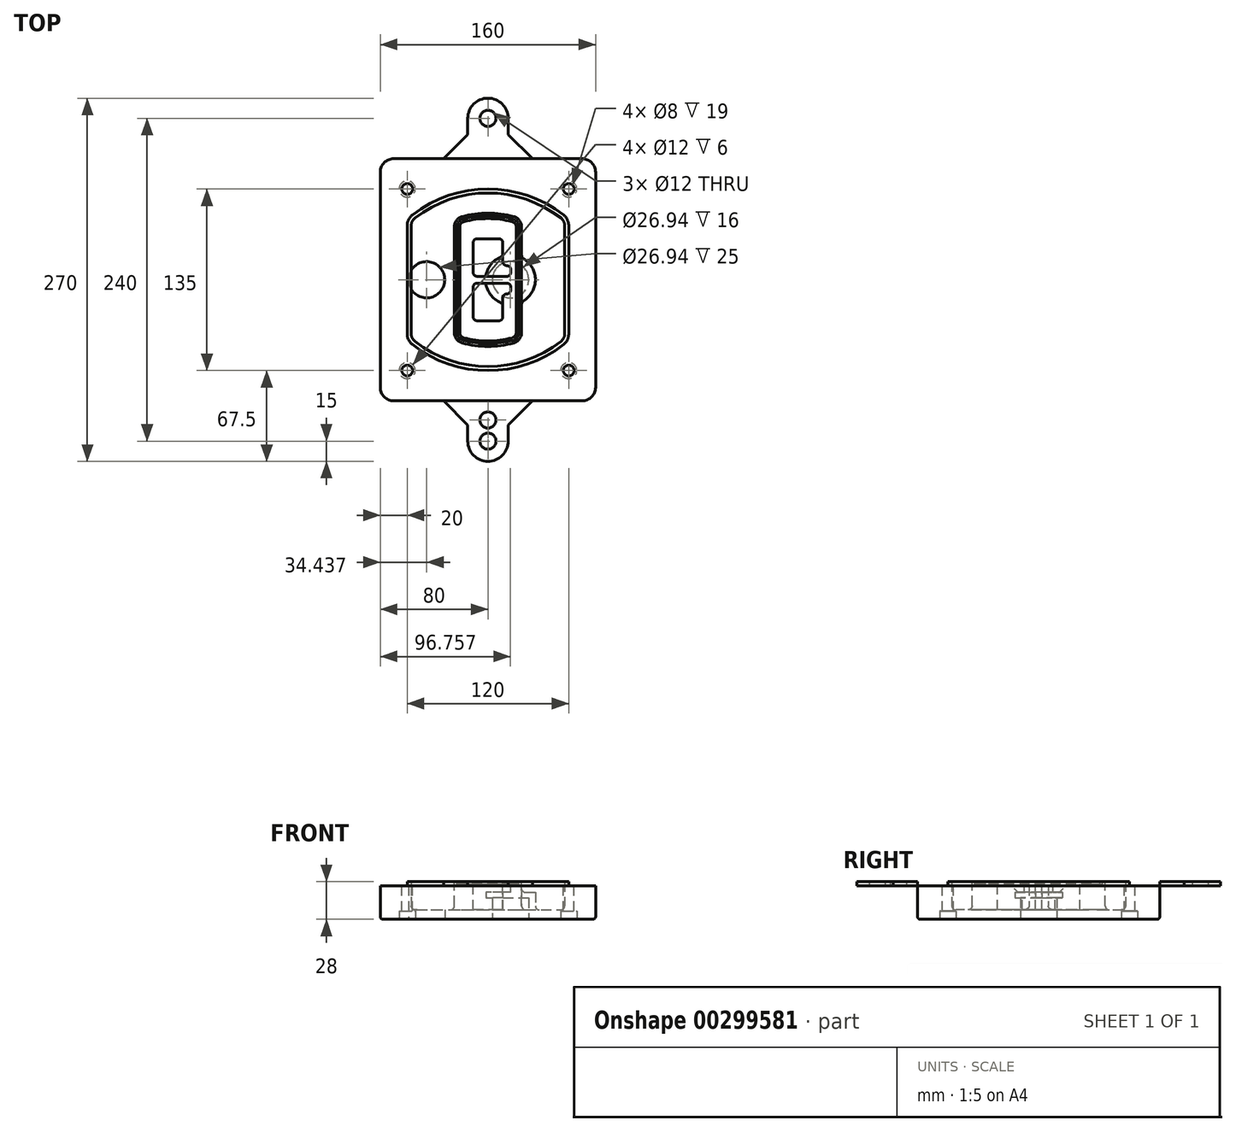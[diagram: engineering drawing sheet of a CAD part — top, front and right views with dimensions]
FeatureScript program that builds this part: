
annotation { "Feature Type Name" : "Feature", "Feature Type Description" : "" }
export const myFeature = defineFeature(function(context is Context, id is Id, definition is map)
    precondition{}
    {
        {
            var Q0;
            Q0=qCreatedBy(makeId("Top.planeOp"),FACE);
            var sketch = newSketch(context, id + "F0", { "sketchPlane" : qUnion([Q0])});
            skPoint(sketch, "E0.rect.middle", {"position": v(0, 0) * mm});
            skLineSegment(sketch, "E1.bottom", {"start": v(-70, -90) * mm, "end": v(70, -90) * mm});
            skLineSegment(sketch, "E1.top", {"start": v(-70, 90) * mm, "end": v(70, 90) * mm});
            skLineSegment(sketch, "E1.left", {"start": v(-80, -80) * mm, "end": v(-80, 80) * mm});
            skLineSegment(sketch, "E1.right", {"start": v(80, -80) * mm, "end": v(80, 80) * mm});
            skLineSegment(sketch, "E2", {"start": v(-80, 90) * mm, "end": v(80, -90) * mm, "construction": true});
            skLineSegment(sketch, "E3", {"start": v(80, 90) * mm, "end": v(-80, -90) * mm, "construction": true});
            skCircle(sketch, "E4", {"center": v(-60, 67.5) * mm, "radius": 4 * mm});
            skCircle(sketch, "E5", {"center": v(60, 67.5) * mm, "radius": 4 * mm});
            skCircle(sketch, "E6", {"center": v(60, -67.5) * mm, "radius": 4 * mm});
            skCircle(sketch, "E7", {"center": v(-60, -67.5) * mm, "radius": 4 * mm});
            skLineSegment(sketch, "E8", {"start": v(-60, 67.5) * mm, "end": v(60, 67.5) * mm, "construction": true});
            skLineSegment(sketch, "E9", {"start": v(60, 67.5) * mm, "end": v(60, -67.5) * mm, "construction": true});
            skLineSegment(sketch, "E10", {"start": v(60, -67.5) * mm, "end": v(-60, -67.5) * mm, "construction": true});
            skLineSegment(sketch, "E11", {"start": v(-60, -67.5) * mm, "end": v(-60, 67.5) * mm, "construction": true});
            skLineSegment(sketch, "E12", {"start": v(-60, 40.3) * mm, "end": v(-60, -40.3) * mm});
            skLineSegment(sketch, "E13", {"start": v(60, 40.3) * mm, "end": v(60, -40.3) * mm});
            skArc(sketch, "E14", {"start": v(56.15, 48.18) * mm, "mid": v(0, 67.5) * mm, "end": v(-56.15, 48.18) * mm});
            skArc(sketch, "E15", {"start": v(-56.15, -48.18) * mm, "mid": v(0, -67.5) * mm, "end": v(56.15, -48.18) * mm});
            skLineSegment(sketch, "E16", {"start": v(-60, 0) * mm, "end": v(60, 0) * mm, "construction": true});
            skPoint(sketch, "E17.visualSharp", {"position": v(-60, -45) * mm});
            skArc(sketch, "E17.filletArc", {"start": v(-60, -40.3) * mm, "mid": v(-58.99, -44.68) * mm, "end": v(-56.15, -48.18) * mm});
            skPoint(sketch, "E18.visualSharp", {"position": v(-60, 45) * mm});
            skArc(sketch, "E18.filletArc", {"start": v(-56.15, 48.18) * mm, "mid": v(-58.99, 44.68) * mm, "end": v(-60, 40.3) * mm});
            skPoint(sketch, "E19.visualSharp", {"position": v(60, 45) * mm});
            skArc(sketch, "E19.filletArc", {"start": v(60, 40.3) * mm, "mid": v(58.99, 44.68) * mm, "end": v(56.15, 48.18) * mm});
            skPoint(sketch, "E20.visualSharp", {"position": v(60, -45) * mm});
            skArc(sketch, "E20.filletArc", {"start": v(56.15, -48.18) * mm, "mid": v(58.99, -44.68) * mm, "end": v(60, -40.3) * mm});
            skPoint(sketch, "E21.visualSharp", {"position": v(-80, 90) * mm});
            skArc(sketch, "E21.filletArc", {"start": v(-70, 90) * mm, "mid": v(-77.07, 87.07) * mm, "end": v(-80, 80) * mm});
            skPoint(sketch, "E22.visualSharp", {"position": v(80, 90) * mm});
            skArc(sketch, "E22.filletArc", {"start": v(80, 80) * mm, "mid": v(77.07, 87.07) * mm, "end": v(70, 90) * mm});
            skPoint(sketch, "E23.visualSharp", {"position": v(80, -90) * mm});
            skArc(sketch, "E23.filletArc", {"start": v(70, -90) * mm, "mid": v(77.07, -87.07) * mm, "end": v(80, -80) * mm});
            skPoint(sketch, "E24.visualSharp", {"position": v(-80, -90) * mm});
            skArc(sketch, "E24.filletArc", {"start": v(-80, -80) * mm, "mid": v(-77.07, -87.07) * mm, "end": v(-70, -90) * mm});
            skArc(sketch, "E25.0", {"start": v(57, 40.3) * mm, "mid": v(56.3, 43.36) * mm, "end": v(54.3, 45.81) * mm});
            skLineSegment(sketch, "E25.1", {"start": v(57, 40.3) * mm, "end": v(57, -40.3) * mm});
            skArc(sketch, "E25.2", {"start": v(54.3, -45.81) * mm, "mid": v(56.3, -43.36) * mm, "end": v(57, -40.3) * mm});
            skArc(sketch, "E25.3", {"start": v(-54.3, -45.81) * mm, "mid": v(0, -64.5) * mm, "end": v(54.3, -45.81) * mm});
            skArc(sketch, "E25.4", {"start": v(-57, -40.3) * mm, "mid": v(-56.3, -43.36) * mm, "end": v(-54.3, -45.81) * mm});
            skArc(sketch, "E25.5", {"start": v(54.3, 45.81) * mm, "mid": v(0, 64.5) * mm, "end": v(-54.3, 45.81) * mm});
            skLineSegment(sketch, "E25.6", {"start": v(-57, 40.3) * mm, "end": v(-57, -40.3) * mm});
            skArc(sketch, "E25.7", {"start": v(-54.3, 45.81) * mm, "mid": v(-56.3, 43.36) * mm, "end": v(-57, 40.3) * mm});
            skArc(sketch, "E26.0", {"start": v(-58.62, 51.33) * mm, "mid": v(-62.58, 46.43) * mm, "end": v(-64, 40.3) * mm});
            skArc(sketch, "E26.1", {"start": v(58.62, 51.33) * mm, "mid": v(0, 71.5) * mm, "end": v(-58.62, 51.33) * mm});
            skArc(sketch, "E26.2", {"start": v(64, 40.3) * mm, "mid": v(62.58, 46.43) * mm, "end": v(58.62, 51.33) * mm});
            skLineSegment(sketch, "E26.3", {"start": v(64, 40.3) * mm, "end": v(64, -40.3) * mm});
            skArc(sketch, "E26.4", {"start": v(58.62, -51.33) * mm, "mid": v(62.58, -46.43) * mm, "end": v(64, -40.3) * mm});
            skLineSegment(sketch, "E26.5", {"start": v(-64, 40.3) * mm, "end": v(-64, -40.3) * mm});
            skArc(sketch, "E26.6", {"start": v(-58.62, -51.33) * mm, "mid": v(0, -71.5) * mm, "end": v(58.62, -51.33) * mm});
            skArc(sketch, "E26.7", {"start": v(-64, -40.3) * mm, "mid": v(-62.58, -46.43) * mm, "end": v(-58.62, -51.33) * mm});
            skSolve(sketch);
        }
        {
            var Q0;
            Q0=makeQuery(id+"F0.imprint","IMPRINT",FACE,{"disambiguationData":[TD([[makeQuery(id+"F0.imprint","IMPRINT",EDGE,{"derivedFrom":sQuery(id+"F0.wireOp",EDGE,"E1.bottom")}),1.0]])]});
            var Q1;
            Q1=makeQuery(id+"F0.imprint","IMPRINT",FACE,{"disambiguationData":[TD([[makeQuery(id+"F0.imprint","IMPRINT",EDGE,{"derivedFrom":sQuery(id+"F0.wireOp",EDGE,"E12")}),1.0]])]});
            var Q2;
            Q2=makeQuery(id+"F0.imprint","IMPRINT",FACE,{"disambiguationData":[TD([[makeQuery(id+"F0.imprint","IMPRINT",EDGE,{"derivedFrom":sQuery(id+"F0.wireOp",EDGE,"E25.0")}),1.0]])]});
            var Q3;
            Q3=makeQuery(id+"F0.imprint","IMPRINT",FACE,{"disambiguationData":[TD([[makeQuery(id+"F0.imprint","IMPRINT",EDGE,{"derivedFrom":sQuery(id+"F0.wireOp",EDGE,"E12")}),-1.0]])]});
            extrude(context, id + "F1", {"entities" : qUnion([Q0, Q1, Q2, Q3]), "oppositeDirection" : true, "depth" : 25 * mm});
        }
        {
            var Q0;
            Q0=makeQuery(id+"F0.imprint","IMPRINT",FACE,{"disambiguationData":[TD([[makeQuery(id+"F0.imprint","IMPRINT",EDGE,{"derivedFrom":sQuery(id+"F0.wireOp",EDGE,"E12")}),1.0]])]});
            extrude(context, id + "F2", {"entities" : qUnion([Q0]), "operationType" : NewBodyOperationType.ADD, "depth" : 3 * mm});
        }
        {
            var Q0;
            Q0=makeQuery(id+"F0.imprint","IMPRINT",FACE,{"disambiguationData":[TD([[makeQuery(id+"F0.imprint","IMPRINT",EDGE,{"derivedFrom":sQuery(id+"F0.wireOp",EDGE,"E25.0")}),1.0]])]});
            extrude(context, id + "F3", {"entities" : qUnion([Q0]), "operationType" : NewBodyOperationType.REMOVE, "oppositeDirection" : true, "depth" : 18 * mm});
        }
        {
            var Q0;
            Q0=makeQuery(id+"F2.opExtrude","CAP_FACE",FACE,{"disambiguationData":[OSD([sQuery(id+"F0.wireOp",EDGE,"E12"),sQuery(id+"F0.wireOp",EDGE,"E13"),sQuery(id+"F0.wireOp",EDGE,"E14"),sQuery(id+"F0.wireOp",EDGE,"E15"),sQuery(id+"F0.wireOp",EDGE,"E17.filletArc"),sQuery(id+"F0.wireOp",EDGE,"E18.filletArc"),sQuery(id+"F0.wireOp",EDGE,"E19.filletArc"),sQuery(id+"F0.wireOp",EDGE,"E20.filletArc"),sQuery(id+"F0.wireOp",EDGE,"E25.0"),sQuery(id+"F0.wireOp",EDGE,"E25.1"),sQuery(id+"F0.wireOp",EDGE,"E25.2"),sQuery(id+"F0.wireOp",EDGE,"E25.3"),sQuery(id+"F0.wireOp",EDGE,"E25.4"),sQuery(id+"F0.wireOp",EDGE,"E25.5"),sQuery(id+"F0.wireOp",EDGE,"E25.6"),sQuery(id+"F0.wireOp",EDGE,"E25.7")])],"isStart":false});
            var sketch = newSketch(context, id + "F4", { "sketchPlane" : qUnion([Q0])});
            skArc(sketch, "E27.0", {"start": v(-19.08, -46.97) * mm, "mid": v(0, -49.5) * mm, "end": v(19.08, -46.97) * mm});
            skArc(sketch, "E28.0", {"start": v(19.08, 46.97) * mm, "mid": v(0, 49.5) * mm, "end": v(-19.08, 46.97) * mm});
            skLineSegment(sketch, "E29", {"start": v(-25, 39.25) * mm, "end": v(-25, -39.25) * mm});
            skLineSegment(sketch, "E30", {"start": v(25, 39.25) * mm, "end": v(25, -39.25) * mm});
            skLineSegment(sketch, "E31", {"start": v(-25, 45.1) * mm, "end": v(25, 45.1) * mm, "construction": true});
            skLineSegment(sketch, "E32", {"start": v(-25, -45.1) * mm, "end": v(25, -45.1) * mm, "construction": true});
            skPoint(sketch, "E33.visualSharp", {"position": v(-25, 45.1) * mm});
            skArc(sketch, "E33.filletArc", {"start": v(-19.08, 46.97) * mm, "mid": v(-23.35, 44.11) * mm, "end": v(-25, 39.25) * mm});
            skPoint(sketch, "E34.visualSharp", {"position": v(25, 45.1) * mm});
            skArc(sketch, "E34.filletArc", {"start": v(25, 39.25) * mm, "mid": v(23.35, 44.11) * mm, "end": v(19.08, 46.97) * mm});
            skPoint(sketch, "E35.visualSharp", {"position": v(25, -45.1) * mm});
            skArc(sketch, "E35.filletArc", {"start": v(19.08, -46.97) * mm, "mid": v(23.35, -44.11) * mm, "end": v(25, -39.25) * mm});
            skPoint(sketch, "E36.visualSharp", {"position": v(-25, -45.1) * mm});
            skArc(sketch, "E36.filletArc", {"start": v(-25, -39.25) * mm, "mid": v(-23.35, -44.11) * mm, "end": v(-19.08, -46.97) * mm});
            skArc(sketch, "E37.0", {"start": v(54.3, 45.81) * mm, "mid": v(0, 64.5) * mm, "end": v(-54.3, 45.81) * mm});
            skArc(sketch, "E37.1", {"start": v(-54.3, 45.81) * mm, "mid": v(-56.3, 43.36) * mm, "end": v(-57, 40.3) * mm});
            skLineSegment(sketch, "E37.2", {"start": v(-57, 40.3) * mm, "end": v(-57, -40.3) * mm});
            skArc(sketch, "E37.3", {"start": v(-57, -40.3) * mm, "mid": v(-56.3, -43.36) * mm, "end": v(-54.3, -45.81) * mm});
            skArc(sketch, "E37.4", {"start": v(-54.3, -45.81) * mm, "mid": v(0, -64.5) * mm, "end": v(54.3, -45.81) * mm});
            skArc(sketch, "E37.5", {"start": v(54.3, -45.81) * mm, "mid": v(56.3, -43.36) * mm, "end": v(57, -40.3) * mm});
            skLineSegment(sketch, "E37.6", {"start": v(57, 40.3) * mm, "end": v(57, -40.3) * mm});
            skArc(sketch, "E37.7", {"start": v(57, 40.3) * mm, "mid": v(56.3, 43.36) * mm, "end": v(54.3, 45.81) * mm});
            skLineSegment(sketch, "E38.0", {"start": v(23, 39.25) * mm, "end": v(23, -39.25) * mm});
            skArc(sketch, "E38.1", {"start": v(18.56, -45.04) * mm, "mid": v(21.76, -42.9) * mm, "end": v(23, -39.25) * mm});
            skArc(sketch, "E38.2", {"start": v(-18.56, -45.04) * mm, "mid": v(0, -47.5) * mm, "end": v(18.56, -45.04) * mm});
            skArc(sketch, "E38.3", {"start": v(-23, -39.25) * mm, "mid": v(-21.76, -42.9) * mm, "end": v(-18.56, -45.04) * mm});
            skLineSegment(sketch, "E38.4", {"start": v(-23, 39.25) * mm, "end": v(-23, -39.25) * mm});
            skArc(sketch, "E38.5", {"start": v(23, 39.25) * mm, "mid": v(21.76, 42.9) * mm, "end": v(18.56, 45.04) * mm});
            skArc(sketch, "E38.6", {"start": v(-18.56, 45.04) * mm, "mid": v(-21.76, 42.9) * mm, "end": v(-23, 39.25) * mm});
            skArc(sketch, "E38.7", {"start": v(18.56, 45.04) * mm, "mid": v(0, 47.5) * mm, "end": v(-18.56, 45.04) * mm});
            skArc(sketch, "E39.0", {"start": v(21, 39.25) * mm, "mid": v(20.18, 41.68) * mm, "end": v(18.04, 43.1) * mm});
            skLineSegment(sketch, "E39.1", {"start": v(21, 39.25) * mm, "end": v(21, -39.25) * mm});
            skArc(sketch, "E39.2", {"start": v(18.04, -43.1) * mm, "mid": v(20.18, -41.68) * mm, "end": v(21, -39.25) * mm});
            skArc(sketch, "E39.3", {"start": v(-18.04, -43.1) * mm, "mid": v(0, -45.5) * mm, "end": v(18.04, -43.1) * mm});
            skArc(sketch, "E39.4", {"start": v(-21, -39.25) * mm, "mid": v(-20.18, -41.68) * mm, "end": v(-18.04, -43.1) * mm});
            skArc(sketch, "E39.5", {"start": v(18.04, 43.1) * mm, "mid": v(0, 45.5) * mm, "end": v(-18.04, 43.1) * mm});
            skLineSegment(sketch, "E39.6", {"start": v(-21, 39.25) * mm, "end": v(-21, -39.25) * mm});
            skArc(sketch, "E39.7", {"start": v(-18.04, 43.1) * mm, "mid": v(-20.18, 41.68) * mm, "end": v(-21, 39.25) * mm});
            skLineSegment(sketch, "E40", {"start": v(-25, 0) * mm, "end": v(25, 0) * mm, "construction": true});
            skLineSegment(sketch, "E41", {"start": v(-11, 5.5) * mm, "end": v(-11, 27.5) * mm});
            skLineSegment(sketch, "E42", {"start": v(-8, 30.5) * mm, "end": v(8, 30.5) * mm});
            skLineSegment(sketch, "E43", {"start": v(11, 27.5) * mm, "end": v(11, 13.5) * mm});
            skLineSegment(sketch, "E44", {"start": v(14, 10.5) * mm, "end": v(14, 10.5) * mm});
            skLineSegment(sketch, "E45", {"start": v(17, 7.5) * mm, "end": v(17, 5.5) * mm});
            skLineSegment(sketch, "E46", {"start": v(14, 2.5) * mm, "end": v(-8, 2.5) * mm});
            skPoint(sketch, "E47.visualSharp", {"position": v(-11, 30.5) * mm});
            skArc(sketch, "E47.filletArc", {"start": v(-8, 30.5) * mm, "mid": v(-10.12, 29.62) * mm, "end": v(-11, 27.5) * mm});
            skPoint(sketch, "E48.visualSharp", {"position": v(11, 30.5) * mm});
            skArc(sketch, "E48.filletArc", {"start": v(11, 27.5) * mm, "mid": v(10.12, 29.62) * mm, "end": v(8, 30.5) * mm});
            skPoint(sketch, "E49.visualSharp", {"position": v(11, 10.5) * mm});
            skArc(sketch, "E49.filletArc", {"start": v(11, 13.5) * mm, "mid": v(11.88, 11.38) * mm, "end": v(14, 10.5) * mm});
            skPoint(sketch, "E50.visualSharp", {"position": v(17, 10.5) * mm});
            skArc(sketch, "E50.filletArc", {"start": v(17, 7.5) * mm, "mid": v(16.12, 9.62) * mm, "end": v(14, 10.5) * mm});
            skPoint(sketch, "E51.visualSharp", {"position": v(17, 2.5) * mm});
            skArc(sketch, "E51.filletArc", {"start": v(14, 2.5) * mm, "mid": v(16.12, 3.38) * mm, "end": v(17, 5.5) * mm});
            skPoint(sketch, "E52.visualSharp", {"position": v(-11, 2.5) * mm});
            skArc(sketch, "E52.filletArc", {"start": v(-11, 5.5) * mm, "mid": v(-10.12, 3.38) * mm, "end": v(-8, 2.5) * mm});
            skLineSegment(sketch, "E53.0.MirrorCS", {"start": v(14, -2.5) * mm, "end": v(-8, -2.5) * mm});
            skArc(sketch, "E54.0.MirrorCS", {"start": v(-11, -5.5) * mm, "mid": v(-10.12, -3.38) * mm, "end": v(-8, -2.5) * mm});
            skLineSegment(sketch, "E55.0.MirrorCS", {"start": v(-11, -5.5) * mm, "end": v(-11, -27.5) * mm});
            skArc(sketch, "E56.0.MirrorCS", {"start": v(-8, -30.5) * mm, "mid": v(-10.12, -29.62) * mm, "end": v(-11, -27.5) * mm});
            skLineSegment(sketch, "E57.0.MirrorCS", {"start": v(-8, -30.5) * mm, "end": v(8, -30.5) * mm});
            skArc(sketch, "E58.0.MirrorCS", {"start": v(11, -27.5) * mm, "mid": v(10.12, -29.62) * mm, "end": v(8, -30.5) * mm});
            skLineSegment(sketch, "E59.0.MirrorCS", {"start": v(11, -27.5) * mm, "end": v(11, -13.5) * mm});
            skArc(sketch, "E60.0.MirrorCS", {"start": v(11, -13.5) * mm, "mid": v(11.88, -11.38) * mm, "end": v(14, -10.5) * mm});
            skArc(sketch, "E61.0.MirrorCS", {"start": v(17, -7.5) * mm, "mid": v(16.12, -9.62) * mm, "end": v(14, -10.5) * mm});
            skLineSegment(sketch, "E62.0.MirrorCS", {"start": v(17, -7.5) * mm, "end": v(17, -5.5) * mm});
            skArc(sketch, "E63.0.MirrorCS", {"start": v(14, -2.5) * mm, "mid": v(16.12, -3.38) * mm, "end": v(17, -5.5) * mm});
            skSolve(sketch);
        }
        {
            var Q0;
            Q0=makeQuery(id+"F4.imprint","IMPRINT",FACE,{"disambiguationData":[TD([[makeQuery(id+"F4.imprint","IMPRINT",EDGE,{"derivedFrom":sQuery(id+"F4.wireOp",EDGE,"E27.0")}),1.0]])]});
            var Q1;
            Q1=makeQuery(id+"F4.imprint","IMPRINT",FACE,{"disambiguationData":[TD([[makeQuery(id+"F4.imprint","IMPRINT",EDGE,{"derivedFrom":sQuery(id+"F4.wireOp",EDGE,"E38.0")}),-1.0]])]});
            var Q2;
            Q2=makeQuery(id+"F4.imprint","IMPRINT",FACE,{"disambiguationData":[TD([[makeQuery(id+"F4.imprint","IMPRINT",EDGE,{"derivedFrom":sQuery(id+"F4.wireOp",EDGE,"E39.0")}),1.0]])]});
            extrude(context, id + "F5", {"entities" : qUnion([Q0, Q1, Q2]), "operationType" : NewBodyOperationType.ADD, "endBound" : BoundingType.UP_TO_NEXT, "oppositeDirection" : true, "depth" : 25 * mm});
        }
        {
            var Q0;
            Q0=makeQuery(id+"F4.imprint","IMPRINT",FACE,{"disambiguationData":[TD([[makeQuery(id+"F4.imprint","IMPRINT",EDGE,{"derivedFrom":sQuery(id+"F4.wireOp",EDGE,"E38.0")}),-1.0]])]});
            extrude(context, id + "F6", {"entities" : qUnion([Q0]), "operationType" : NewBodyOperationType.REMOVE, "oppositeDirection" : true, "depth" : 2 * mm});
        }
        {
            var Q0;
            Q0=makeQuery(id+"F1.opExtrude","CAP_FACE",FACE,{"disambiguationData":[OSD([sQuery(id+"F0.wireOp",EDGE,"E1.bottom"),sQuery(id+"F0.wireOp",EDGE,"E1.top"),sQuery(id+"F0.wireOp",EDGE,"E1.left"),sQuery(id+"F0.wireOp",EDGE,"E1.right"),sQuery(id+"F0.wireOp",EDGE,"E4"),sQuery(id+"F0.wireOp",EDGE,"E5"),sQuery(id+"F0.wireOp",EDGE,"E6"),sQuery(id+"F0.wireOp",EDGE,"E7"),sQuery(id+"F0.wireOp",EDGE,"E21.filletArc"),sQuery(id+"F0.wireOp",EDGE,"E22.filletArc"),sQuery(id+"F0.wireOp",EDGE,"E23.filletArc"),sQuery(id+"F0.wireOp",EDGE,"E24.filletArc")])],"isStart":false});
            var sketch = newSketch(context, id + "F7", { "sketchPlane" : qUnion([Q0])});
            skCircle(sketch, "E64", {"center": v(16.76, 0) * mm, "radius": 13.47 * mm});
            skCircle(sketch, "E65", {"center": v(-45.56, 0) * mm, "radius": 13.47 * mm});
            skLineSegment(sketch, "E66", {"start": v(80, 0) * mm, "end": v(-80, 0) * mm});
            skCircle(sketch, "E67", {"center": v(16.76, 0) * mm, "radius": 18.47 * mm});
            skCircle(sketch, "E68", {"center": v(60, -67.5) * mm, "radius": 6 * mm});
            skCircle(sketch, "E69", {"center": v(-60, -67.5) * mm, "radius": 6 * mm});
            skCircle(sketch, "E70", {"center": v(-60, 67.5) * mm, "radius": 6 * mm});
            skCircle(sketch, "E71", {"center": v(60, 67.5) * mm, "radius": 6 * mm});
            skSolve(sketch);
        }
        {
            var Q0;
            {var subQ1=sQuery(id+"F7.wireOp",EDGE,"E66");var subQ4=sQuery(id+"F7.wireOp",EDGE,"E64");var subQ6=makeQuery(id+"F7.imprint","INTERSECT",VERTEX,{"disambiguationData":[OD(0.0)],"derivedFrom":[subQ4,subQ1]});Q0=makeQuery(id+"F7.imprint","IMPRINT",FACE,{"disambiguationData":[TD([[makeQuery(id+"F7.imprint","IMPRINT",EDGE,{"disambiguationData":[TD([[subQ6,-1.0]])],"derivedFrom":subQ4}),-1.0]])]});}
            var Q1;
            {var subQ0=sQuery(id+"F7.wireOp",EDGE,"E66");var subQ1=sQuery(id+"F7.wireOp",EDGE,"E64");var subQ3=makeQuery(id+"F7.imprint","INTERSECT",VERTEX,{"disambiguationData":[OD(0.0)],"derivedFrom":[subQ1,subQ0]});Q1=makeQuery(id+"F7.imprint","IMPRINT",FACE,{"disambiguationData":[TD([[makeQuery(id+"F7.imprint","IMPRINT",EDGE,{"disambiguationData":[TD([[subQ3,-1.0]])],"derivedFrom":subQ1}),1.0]])]});}
            var Q2;
            {var subQ0=sQuery(id+"F7.wireOp",EDGE,"E66");var subQ1=sQuery(id+"F7.wireOp",EDGE,"E64");var subQ3=makeQuery(id+"F7.imprint","INTERSECT",VERTEX,{"disambiguationData":[OD(0.0)],"derivedFrom":[subQ1,subQ0]});Q2=makeQuery(id+"F7.imprint","IMPRINT",FACE,{"disambiguationData":[TD([[makeQuery(id+"F7.imprint","IMPRINT",EDGE,{"disambiguationData":[TD([[subQ3,1.0]])],"derivedFrom":subQ1}),1.0]])]});}
            var Q3;
            {var subQ1=sQuery(id+"F7.wireOp",EDGE,"E66");var subQ4=sQuery(id+"F7.wireOp",EDGE,"E64");var subQ6=makeQuery(id+"F7.imprint","INTERSECT",VERTEX,{"disambiguationData":[OD(0.0)],"derivedFrom":[subQ4,subQ1]});Q3=makeQuery(id+"F7.imprint","IMPRINT",FACE,{"disambiguationData":[TD([[makeQuery(id+"F7.imprint","IMPRINT",EDGE,{"disambiguationData":[TD([[subQ6,1.0]])],"derivedFrom":subQ4}),-1.0]])]});}
            extrude(context, id + "F8", {"entities" : qUnion([Q0, Q1, Q2, Q3]), "operationType" : NewBodyOperationType.ADD, "oppositeDirection" : true, "depth" : 20 * mm});
        }
        {
            var Q0;
            {var subQ0=sQuery(id+"F7.wireOp",EDGE,"E66");var subQ1=sQuery(id+"F7.wireOp",EDGE,"E64");var subQ3=makeQuery(id+"F7.imprint","INTERSECT",VERTEX,{"disambiguationData":[OD(0.0)],"derivedFrom":[subQ1,subQ0]});Q0=makeQuery(id+"F7.imprint","IMPRINT",FACE,{"disambiguationData":[TD([[makeQuery(id+"F7.imprint","IMPRINT",EDGE,{"disambiguationData":[TD([[subQ3,-1.0]])],"derivedFrom":subQ1}),1.0]])]});}
            var Q1;
            {var subQ0=sQuery(id+"F7.wireOp",EDGE,"E66");var subQ1=sQuery(id+"F7.wireOp",EDGE,"E64");var subQ3=makeQuery(id+"F7.imprint","INTERSECT",VERTEX,{"disambiguationData":[OD(0.0)],"derivedFrom":[subQ1,subQ0]});Q1=makeQuery(id+"F7.imprint","IMPRINT",FACE,{"disambiguationData":[TD([[makeQuery(id+"F7.imprint","IMPRINT",EDGE,{"disambiguationData":[TD([[subQ3,1.0]])],"derivedFrom":subQ1}),1.0]])]});}
            extrude(context, id + "F9", {"entities" : qUnion([Q0, Q1]), "operationType" : NewBodyOperationType.REMOVE, "oppositeDirection" : true, "depth" : 16 * mm});
        }
        {
            var Q0;
            {var subQ0=sQuery(id+"F7.wireOp",EDGE,"E66");var subQ1=sQuery(id+"F7.wireOp",EDGE,"E65");var subQ3=makeQuery(id+"F7.imprint","INTERSECT",VERTEX,{"disambiguationData":[OD(0.0)],"derivedFrom":[subQ1,subQ0]});Q0=makeQuery(id+"F7.imprint","IMPRINT",FACE,{"disambiguationData":[TD([[makeQuery(id+"F7.imprint","IMPRINT",EDGE,{"disambiguationData":[TD([[subQ3,-1.0]])],"derivedFrom":subQ1}),1.0]])]});}
            var Q1;
            {var subQ0=sQuery(id+"F7.wireOp",EDGE,"E66");var subQ1=sQuery(id+"F7.wireOp",EDGE,"E65");var subQ3=makeQuery(id+"F7.imprint","INTERSECT",VERTEX,{"disambiguationData":[OD(0.0)],"derivedFrom":[subQ1,subQ0]});Q1=makeQuery(id+"F7.imprint","IMPRINT",FACE,{"disambiguationData":[TD([[makeQuery(id+"F7.imprint","IMPRINT",EDGE,{"disambiguationData":[TD([[subQ3,1.0]])],"derivedFrom":subQ1}),1.0]])]});}
            extrude(context, id + "F10", {"entities" : qUnion([Q0, Q1]), "operationType" : NewBodyOperationType.REMOVE, "oppositeDirection" : true, "depth" : 25 * mm});
        }
        {
            var Q0;
            Q0=makeQuery(id+"F7.imprint","IMPRINT",FACE,{"disambiguationData":[TD([[makeQuery(id+"F7.imprint","IMPRINT",EDGE,{"derivedFrom":sQuery(id+"F7.wireOp",EDGE,"E68")}),1.0]])]});
            var Q1;
            Q1=makeQuery(id+"F7.imprint","IMPRINT",FACE,{"disambiguationData":[TD([[makeQuery(id+"F7.imprint","IMPRINT",EDGE,{"derivedFrom":makeQuery(id+"F1.opExtrude","CAP_EDGE",EDGE,{"disambiguationData":[OSD([sQuery(id+"F0.wireOp",EDGE,"E5")])],"isStart":false})}),-1.0]])]});
            var Q2;
            Q2=makeQuery(id+"F7.imprint","IMPRINT",FACE,{"disambiguationData":[TD([[makeQuery(id+"F7.imprint","IMPRINT",EDGE,{"derivedFrom":sQuery(id+"F7.wireOp",EDGE,"E69")}),1.0]])]});
            var Q3;
            Q3=makeQuery(id+"F7.imprint","IMPRINT",FACE,{"disambiguationData":[TD([[makeQuery(id+"F7.imprint","IMPRINT",EDGE,{"derivedFrom":makeQuery(id+"F1.opExtrude","CAP_EDGE",EDGE,{"disambiguationData":[OSD([sQuery(id+"F0.wireOp",EDGE,"E4")])],"isStart":false})}),-1.0]])]});
            var Q4;
            Q4=makeQuery(id+"F7.imprint","IMPRINT",FACE,{"disambiguationData":[TD([[makeQuery(id+"F7.imprint","IMPRINT",EDGE,{"derivedFrom":sQuery(id+"F7.wireOp",EDGE,"E70")}),1.0]])]});
            var Q5;
            Q5=makeQuery(id+"F7.imprint","IMPRINT",FACE,{"disambiguationData":[TD([[makeQuery(id+"F7.imprint","IMPRINT",EDGE,{"derivedFrom":makeQuery(id+"F1.opExtrude","CAP_EDGE",EDGE,{"disambiguationData":[OSD([sQuery(id+"F0.wireOp",EDGE,"E7")])],"isStart":false})}),-1.0]])]});
            var Q6;
            Q6=makeQuery(id+"F7.imprint","IMPRINT",FACE,{"disambiguationData":[TD([[makeQuery(id+"F7.imprint","IMPRINT",EDGE,{"derivedFrom":sQuery(id+"F7.wireOp",EDGE,"E71")}),1.0]])]});
            var Q7;
            Q7=makeQuery(id+"F7.imprint","IMPRINT",FACE,{"disambiguationData":[TD([[makeQuery(id+"F7.imprint","IMPRINT",EDGE,{"derivedFrom":makeQuery(id+"F1.opExtrude","CAP_EDGE",EDGE,{"disambiguationData":[OSD([sQuery(id+"F0.wireOp",EDGE,"E6")])],"isStart":false})}),-1.0]])]});
            extrude(context, id + "F11", {"entities" : qUnion([Q0, Q1, Q2, Q3, Q4, Q5, Q6, Q7]), "operationType" : NewBodyOperationType.REMOVE, "oppositeDirection" : true, "depth" : 6 * mm});
        }
        {
            var Q0;
            Q0=makeQuery(id+"F9.boolean.opBoolean","COPY",FACE,{"derivedFrom":makeQuery(id+"F9.opExtrude","CAP_FACE",FACE,{"disambiguationData":[OSD([sQuery(id+"F7.wireOp",EDGE,"E64")])],"isStart":false})});
            var sketch = newSketch(context, id + "F12", { "sketchPlane" : qUnion([Q0])});
            skArc(sketch, "E72.0", {"start": v(11, 17.55) * mm, "mid": v(2.57, 11.82) * mm, "end": v(-1.54, 2.5) * mm});
            skArc(sketch, "E72.1", {"start": v(-1.54, -2.5) * mm, "mid": v(2.57, -11.82) * mm, "end": v(11, -17.55) * mm});
            skLineSegment(sketch, "E73", {"start": v(-1.54, -2.5) * mm, "end": v(14, -2.5) * mm});
            skLineSegment(sketch, "E74.0", {"start": v(14, 2.5) * mm, "end": v(-1.54, 2.5) * mm});
            skArc(sketch, "E74.1", {"start": v(14, 2.5) * mm, "mid": v(16.12, 3.38) * mm, "end": v(17, 5.5) * mm});
            skLineSegment(sketch, "E74.2", {"start": v(17, 7.5) * mm, "end": v(17, 5.5) * mm});
            skArc(sketch, "E74.3", {"start": v(17, 7.5) * mm, "mid": v(16.12, 9.62) * mm, "end": v(14, 10.5) * mm});
            skArc(sketch, "E74.4", {"start": v(11, 13.5) * mm, "mid": v(11.88, 11.38) * mm, "end": v(14, 10.5) * mm});
            skLineSegment(sketch, "E74.5", {"start": v(11, 17.55) * mm, "end": v(11, 13.5) * mm});
            skLineSegment(sketch, "E74.7", {"start": v(14, -2.5) * mm, "end": v(-1.54, -2.5) * mm});
            skArc(sketch, "E74.8", {"start": v(14, -2.5) * mm, "mid": v(16.12, -3.38) * mm, "end": v(17, -5.5) * mm});
            skLineSegment(sketch, "E74.9", {"start": v(17, -7.5) * mm, "end": v(17, -5.5) * mm});
            skArc(sketch, "E74.10", {"start": v(17, -7.5) * mm, "mid": v(16.12, -9.62) * mm, "end": v(14, -10.5) * mm});
            skArc(sketch, "E74.11", {"start": v(11, -13.5) * mm, "mid": v(11.88, -11.38) * mm, "end": v(14, -10.5) * mm});
            skLineSegment(sketch, "E74.12", {"start": v(11, -17.55) * mm, "end": v(11, -13.5) * mm});
            skPoint(sketch, "E75.orphan", {"position": v(11, -27.5) * mm});
            skPoint(sketch, "E76.orphan", {"position": v(-8, -2.5) * mm});
            skPoint(sketch, "E77.orphan", {"position": v(-8, 2.5) * mm});
            skPoint(sketch, "E78.orphan", {"position": v(11, 27.5) * mm});
            skSolve(sketch);
        }
        {
            var Q0;
            {var subQ7=sQuery(id+"F12.wireOp",EDGE,"E72.0");var subQ14=sQuery(id+"F12.wireOp",EDGE,"E72.1");var subQ16=sQuery(id+"F12.wireOp",EDGE,"E74.1");var subQ18=sQuery(id+"F12.wireOp",EDGE,"E74.8");Q0=qUnion([makeQuery(id+"F12.imprint","IMPRINT",FACE,{"disambiguationData":[TD([[makeQuery(id+"F12.imprint","IMPRINT",EDGE,{"derivedFrom":subQ7}),1.0]])]}),makeQuery(id+"F12.imprint","IMPRINT",FACE,{"disambiguationData":[TD([[makeQuery(id+"F12.imprint","IMPRINT",EDGE,{"derivedFrom":subQ14}),1.0]])]}),makeQuery(id+"F12.imprint","IMPRINT",FACE,{"disambiguationData":[TD([[makeQuery(id+"F12.imprint","IMPRINT",EDGE,{"derivedFrom":subQ16}),1.0]])]}),makeQuery(id+"F12.imprint","IMPRINT",FACE,{"disambiguationData":[TD([[makeQuery(id+"F12.imprint","IMPRINT",EDGE,{"derivedFrom":subQ18}),-1.0]])]})]);}
            var Q1;
            Q1=makeQuery(id+"F5.boolean.opBoolean","SPLIT",FACE,{"disambiguationData":[TD([makeQuery(id+"F5.opExtrude","SWEPT_FACE",FACE,{"disambiguationData":[OSD([sQuery(id+"F4.wireOp",EDGE,"E41")])]})])],"derivedFrom":makeQuery(id+"F3.boolean.opBoolean","COPY",FACE,{"derivedFrom":makeQuery(id+"F3.opExtrude","CAP_FACE",FACE,{"disambiguationData":[OSD([sQuery(id+"F0.wireOp",EDGE,"E25.0"),sQuery(id+"F0.wireOp",EDGE,"E25.1"),sQuery(id+"F0.wireOp",EDGE,"E25.2"),sQuery(id+"F0.wireOp",EDGE,"E25.3"),sQuery(id+"F0.wireOp",EDGE,"E25.4"),sQuery(id+"F0.wireOp",EDGE,"E25.5"),sQuery(id+"F0.wireOp",EDGE,"E25.6"),sQuery(id+"F0.wireOp",EDGE,"E25.7")])],"isStart":false})})});
            extrude(context, id + "F13", {"entities" : qUnion([Q0]), "operationType" : NewBodyOperationType.REMOVE, "endBound" : BoundingType.UP_TO_SURFACE, "endBoundEntityFace" : qUnion([Q1]), "depth" : 25 * mm});
        }
        {
            var Q0;
            Q0=makeQuery(id+"F3.boolean.opBoolean","COPY",EDGE,{"derivedFrom":makeQuery(id+"F3.opExtrude","CAP_EDGE",EDGE,{"disambiguationData":[OSD([sQuery(id+"F0.wireOp",EDGE,"E25.6")])],"isStart":false})});
            var Q1;
            Q1=makeQuery(id+"F8.boolean.opBoolean","INTERSECT",EDGE,{"derivedFrom":[makeQuery(id+"F5.opExtrude","SWEPT_FACE",FACE,{"disambiguationData":[OSD([sQuery(id+"F4.wireOp",EDGE,"E30")])]}),makeQuery(id+"F8.opExtrude","CAP_FACE",FACE,{"disambiguationData":[OSD([sQuery(id+"F7.wireOp",EDGE,"E67")])],"isStart":false})]});
            var Q2;
            Q2=makeQuery(id+"F8.boolean.opBoolean","INTERSECT",EDGE,{"disambiguationData":[OD(1.0)],"derivedFrom":[makeQuery(id+"F5.opExtrude","SWEPT_FACE",FACE,{"disambiguationData":[OSD([sQuery(id+"F4.wireOp",EDGE,"E30")])]}),makeQuery(id+"F8.opExtrude","SWEPT_FACE",FACE,{"disambiguationData":[OSD([sQuery(id+"F7.wireOp",EDGE,"E67")])]})]});
            var Q3;
            {var subQ0=sQuery(id+"F4.wireOp",EDGE,"E30");Q3=makeQuery(id+"F8.boolean.opBoolean","SPLIT",EDGE,{"disambiguationData":[TD([makeQuery(id+"F5.opExtrude","SWEPT_FACE",FACE,{"disambiguationData":[OSD([sQuery(id+"F4.wireOp",EDGE,"E35.filletArc")])]})])],"derivedFrom":makeQuery(id+"F5.opExtrude","CAP_EDGE",EDGE,{"disambiguationData":[OSD([subQ0])],"isStart":false})});}
            var Q4;
            {var subQ0=sQuery(id+"F0.wireOp",EDGE,"E25.7");var subQ1=sQuery(id+"F0.wireOp",EDGE,"E25.1");var subQ2=sQuery(id+"F0.wireOp",EDGE,"E25.6");var subQ3=sQuery(id+"F0.wireOp",EDGE,"E25.5");var subQ4=sQuery(id+"F0.wireOp",EDGE,"E25.4");var subQ5=sQuery(id+"F0.wireOp",EDGE,"E25.0");var subQ6=sQuery(id+"F0.wireOp",EDGE,"E25.2");var subQ7=sQuery(id+"F0.wireOp",EDGE,"E25.3");Q4=makeQuery(id+"F8.boolean.opBoolean","INTERSECT",EDGE,{"derivedFrom":[makeQuery(id+"F5.boolean.opBoolean","SPLIT",FACE,{"disambiguationData":[TD([makeQuery(id+"F2.opExtrude","SWEPT_FACE",FACE,{"disambiguationData":[OSD([subQ5])]})])],"derivedFrom":makeQuery(id+"F3.boolean.opBoolean","COPY",FACE,{"derivedFrom":makeQuery(id+"F3.opExtrude","CAP_FACE",FACE,{"disambiguationData":[OSD([subQ5,subQ1,subQ6,subQ7,subQ4,subQ3,subQ2,subQ0])],"isStart":false})})}),makeQuery(id+"F8.opExtrude","SWEPT_FACE",FACE,{"disambiguationData":[OSD([sQuery(id+"F7.wireOp",EDGE,"E67")])]})]});}
            var Q5;
            Q5=makeQuery(id+"F8.boolean.opBoolean","INTERSECT",EDGE,{"disambiguationData":[OD(0.0)],"derivedFrom":[makeQuery(id+"F5.opExtrude","SWEPT_FACE",FACE,{"disambiguationData":[OSD([sQuery(id+"F4.wireOp",EDGE,"E30")])]}),makeQuery(id+"F8.opExtrude","SWEPT_FACE",FACE,{"disambiguationData":[OSD([sQuery(id+"F7.wireOp",EDGE,"E67")])]})]});
            fillet(context, id + "F14", {"entities" : qUnion([Q0, Q1, Q2, Q3, Q4, Q5]), "radius" : 3 * mm, "tangentPropagation" : true, "allowEdgeOverflow" : false});
        }
        {
            var Q0;
            Q0=makeQuery(id+"F1.opExtrude","CAP_EDGE",EDGE,{"disambiguationData":[OSD([sQuery(id+"F0.wireOp",EDGE,"E1.bottom")])],"isStart":false});
            fillet(context, id + "F15", {"entities" : qUnion([Q0]), "radius" : 2 * mm, "tangentPropagation" : true, "allowEdgeOverflow" : false});
        }
        {
            var Q0;
            {var subQ0=sQuery(id+"F0.wireOp",EDGE,"E21.filletArc");var subQ1=sQuery(id+"F0.wireOp",EDGE,"E7");var subQ2=sQuery(id+"F0.wireOp",EDGE,"E6");var subQ3=sQuery(id+"F0.wireOp",EDGE,"E5");var subQ4=sQuery(id+"F0.wireOp",EDGE,"E4");var subQ5=sQuery(id+"F0.wireOp",EDGE,"E22.filletArc");var subQ6=sQuery(id+"F0.wireOp",EDGE,"E1.bottom");var subQ7=sQuery(id+"F0.wireOp",EDGE,"E1.right");var subQ8=sQuery(id+"F0.wireOp",EDGE,"E1.top");var subQ9=sQuery(id+"F0.wireOp",EDGE,"E1.left");var subQ10=sQuery(id+"F0.wireOp",EDGE,"E23.filletArc");var subQ11=sQuery(id+"F0.wireOp",EDGE,"E24.filletArc");Q0=makeQuery(id+"F2.boolean.opBoolean","SPLIT",FACE,{"disambiguationData":[TD([makeQuery(id+"F1.opExtrude","SWEPT_FACE",FACE,{"disambiguationData":[OSD([subQ6])]})])],"derivedFrom":makeQuery(id+"F1.opExtrude","CAP_FACE",FACE,{"disambiguationData":[OSD([subQ6,subQ8,subQ9,subQ7,subQ4,subQ3,subQ2,subQ1,subQ0,subQ5,subQ10,subQ11])],"isStart":true})});}
            var sketch = newSketch(context, id + "F16", { "sketchPlane" : qUnion([Q0])});
            skLineSegment(sketch, "E79", {"start": v(0, 90) * mm, "end": v(0, 120) * mm, "construction": true});
            skArc(sketch, "E80", {"start": v(15, 120) * mm, "mid": v(0, 135) * mm, "end": v(-15, 120) * mm});
            skLineSegment(sketch, "E81", {"start": v(-80, 0) * mm, "end": v(80, 0) * mm, "construction": true});
            skArc(sketch, "E82.MirrorCS", {"start": v(15, -120) * mm, "mid": v(0, -135) * mm, "end": v(-15, -120) * mm});
            skCircle(sketch, "E83.MirrorC", {"center": v(0, -104.25) * mm, "radius": 6 * mm});
            skLineSegment(sketch, "E84.MirrorCS", {"start": v(0, -90) * mm, "end": v(0, -120) * mm, "construction": true});
            skLineSegment(sketch, "E85.MirrorCS", {"start": v(-15, -120) * mm, "end": v(-15, -108) * mm});
            skLineSegment(sketch, "E86.MirrorCS", {"start": v(15, -120) * mm, "end": v(15, -108) * mm});
            skLineSegment(sketch, "E87.MirrorCS", {"start": v(15, -92.25) * mm, "end": v(33, -74.25) * mm});
            skLineSegment(sketch, "E88.MirrorCS", {"start": v(-15, -92.25) * mm, "end": v(-33, -74.25) * mm});
            skLineSegment(sketch, "E89", {"start": v(-15, 120) * mm, "end": v(-15, 108) * mm});
            skLineSegment(sketch, "E90", {"start": v(-15, 108) * mm, "end": v(-33, 90) * mm});
            skLineSegment(sketch, "E91", {"start": v(15, 120) * mm, "end": v(15, 108) * mm});
            skLineSegment(sketch, "E92", {"start": v(15, 108) * mm, "end": v(33, 90) * mm});
            skCircle(sketch, "E93", {"center": v(0, 120) * mm, "radius": 6 * mm});
            skLineSegment(sketch, "E94", {"start": v(-33, 90) * mm, "end": v(33, 90) * mm});
            skLineSegment(sketch, "E95.MirrorCS", {"start": v(-15, -108) * mm, "end": v(-33, -90) * mm});
            skLineSegment(sketch, "E96.MirrorCS", {"start": v(15, -108) * mm, "end": v(33, -90) * mm});
            skLineSegment(sketch, "E97.MirrorCS", {"start": v(-33, -90) * mm, "end": v(33, -90) * mm});
            skCircle(sketch, "E98.MirrorC", {"center": v(0, -120) * mm, "radius": 6 * mm});
            skSolve(sketch);
        }
        {
            var Q0;
            Q0 = qSketchRegion(id + "F16", true);
            var Q1;
            Q1=makeQuery(id+"F2.opExtrude","CAP_FACE",FACE,{"disambiguationData":[OSD([sQuery(id+"F0.wireOp",EDGE,"E12"),sQuery(id+"F0.wireOp",EDGE,"E13"),sQuery(id+"F0.wireOp",EDGE,"E14"),sQuery(id+"F0.wireOp",EDGE,"E15"),sQuery(id+"F0.wireOp",EDGE,"E17.filletArc"),sQuery(id+"F0.wireOp",EDGE,"E18.filletArc"),sQuery(id+"F0.wireOp",EDGE,"E19.filletArc"),sQuery(id+"F0.wireOp",EDGE,"E20.filletArc"),sQuery(id+"F0.wireOp",EDGE,"E25.0"),sQuery(id+"F0.wireOp",EDGE,"E25.1"),sQuery(id+"F0.wireOp",EDGE,"E25.2"),sQuery(id+"F0.wireOp",EDGE,"E25.3"),sQuery(id+"F0.wireOp",EDGE,"E25.4"),sQuery(id+"F0.wireOp",EDGE,"E25.5"),sQuery(id+"F0.wireOp",EDGE,"E25.6"),sQuery(id+"F0.wireOp",EDGE,"E25.7")])],"isStart":false});
            extrude(context, id + "F17", {"entities" : qUnion([Q0]), "endBound" : BoundingType.UP_TO_SURFACE, "endBoundEntityFace" : qUnion([Q1]), "depth" : 25 * mm});
        }
    });
